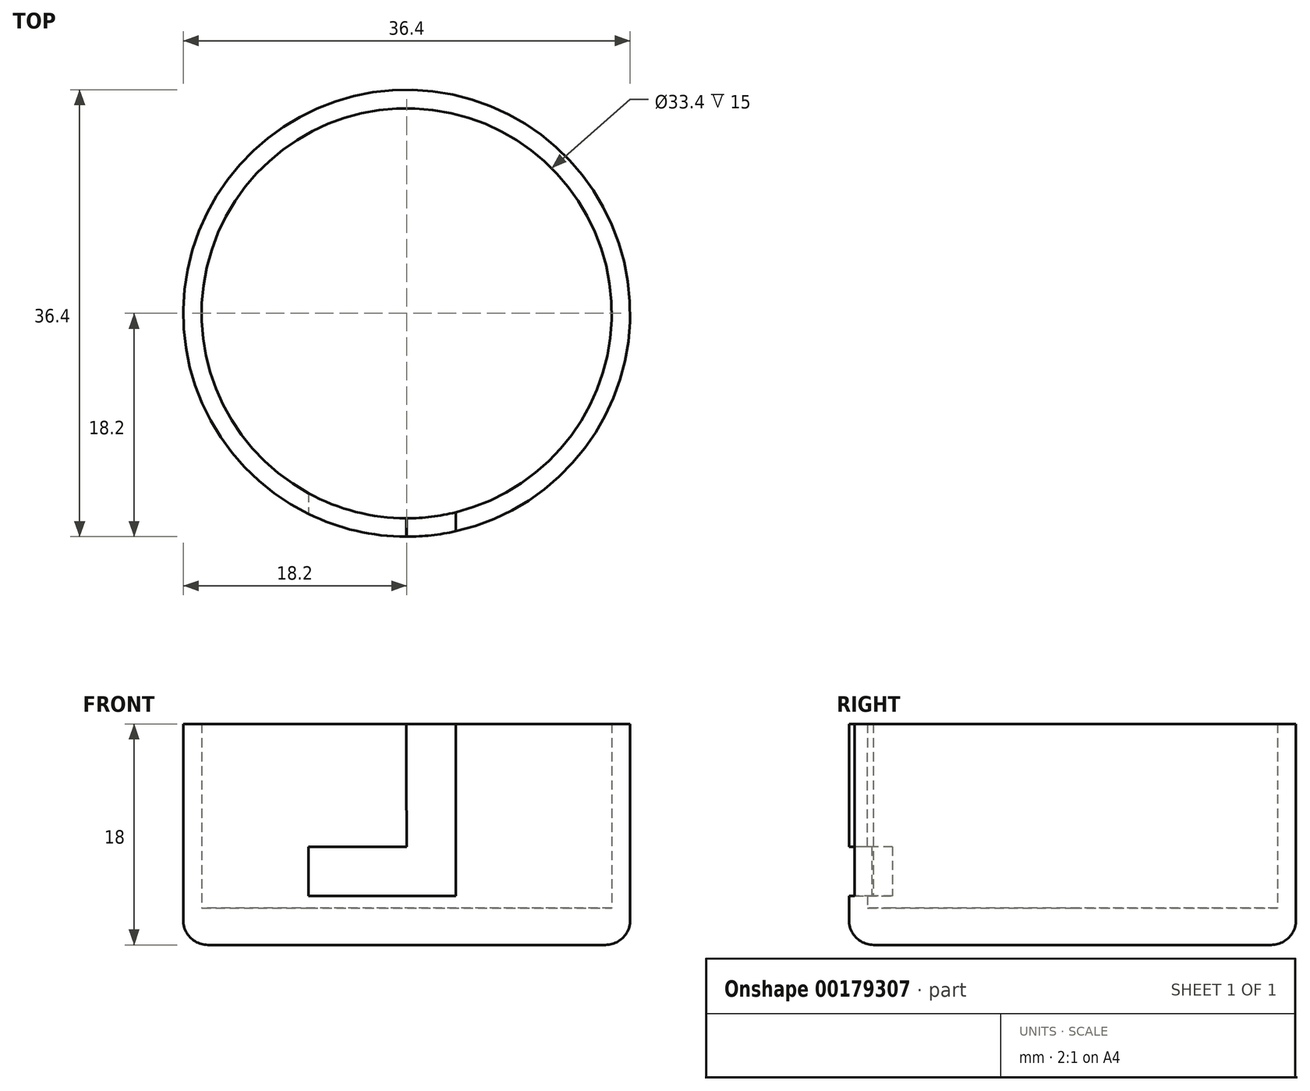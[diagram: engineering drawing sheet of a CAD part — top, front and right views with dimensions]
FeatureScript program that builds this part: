
annotation { "Feature Type Name" : "Feature", "Feature Type Description" : "" }
export const myFeature = defineFeature(function(context is Context, id is Id, definition is map)
    precondition{}
    {
        {
            var Q0;
            Q0=qCreatedBy(makeId("Top.planeOp"),FACE);
            var sketch = newSketch(context, id + "F0", { "sketchPlane" : qUnion([Q0])});
            skCircle(sketch, "E0", {"center": v(0, 0) * mm, "radius": 16.7 * mm});
            skCircle(sketch, "E1", {"center": v(0, 0) * mm, "radius": 18.2 * mm});
            skSolve(sketch);
        }
        {
            var Q0;
            Q0=makeQuery(id+"F0.imprint","IMPRINT",FACE,{"disambiguationData":[TD([[makeQuery(id+"F0.imprint","IMPRINT",EDGE,{"derivedFrom":sQuery(id+"F0.wireOp",EDGE,"E0")}),-1.0]])]});
            var Q1;
            Q1=makeQuery(id+"F0.imprint","IMPRINT",FACE,{"disambiguationData":[TD([[makeQuery(id+"F0.imprint","IMPRINT",EDGE,{"derivedFrom":sQuery(id+"F0.wireOp",EDGE,"E0")}),1.0]])]});
            extrude(context, id + "F1", {"entities" : qUnion([Q0, Q1]), "depth" : 3 * mm});
        }
        {
            var Q0;
            Q0=makeQuery(id+"F1.opExtrude","CAP_FACE",FACE,{"disambiguationData":[OSD([sQuery(id+"F0.wireOp",EDGE,"E1")])],"isStart":false});
            var sketch = newSketch(context, id + "F2", { "sketchPlane" : qUnion([Q0])});
            skCircle(sketch, "E2", {"center": v(0, 0) * mm, "radius": 16.7 * mm});
            skSolve(sketch);
        }
        {
            var Q0;
            Q0=makeQuery(id+"F2.imprint","IMPRINT",FACE,{"disambiguationData":[TD([[makeQuery(id+"F2.imprint","IMPRINT",EDGE,{"derivedFrom":sQuery(id+"F2.wireOp",EDGE,"E2")}),-1.0]])]});
            extrude(context, id + "F3", {"entities" : qUnion([Q0]), "operationType" : NewBodyOperationType.ADD, "depth" : 15 * mm});
        }
        {
            var Q0;
            Q0=qCreatedBy(makeId("Front.planeOp"),FACE);
            cPlane(context, id + "F4", {"entities" : qUnion([Q0]), "cplaneType" : CPlaneType.OFFSET, "offset" : 18.2 * mm, "width" : 150 * mm, "height" : 150 * mm});
        }
        {
            var Q0;
            Q0=qCreatedBy(id+"F4.planeOp",FACE);
            var sketch = newSketch(context, id + "F5", { "sketchPlane" : qUnion([Q0])});
            skLineSegment(sketch, "E3", {"start": v(0, 42.53) * mm, "end": v(0, -15.02) * mm, "construction": true});
            skLineSegment(sketch, "E4", {"start": v(0, 8) * mm, "end": v(-8, 8) * mm});
            skLineSegment(sketch, "E5", {"start": v(-8, 8) * mm, "end": v(-8, 4) * mm});
            skLineSegment(sketch, "E6", {"start": v(-8, 4) * mm, "end": v(4, 4) * mm});
            skLineSegment(sketch, "E7", {"start": v(4, 4) * mm, "end": v(4, 20) * mm});
            skLineSegment(sketch, "E8", {"start": v(-0.04, 16) * mm, "end": v(0, 8) * mm});
            skLineSegment(sketch, "E9", {"start": v(-0.04, 16) * mm, "end": v(-0.04, 20) * mm});
            skLineSegment(sketch, "E10", {"start": v(-0.04, 20) * mm, "end": v(3.96, 20) * mm});
            skLineSegment(sketch, "E11", {"start": v(3.96, 20) * mm, "end": v(4, 20) * mm});
            skSolve(sketch);
        }
        {
            var Q0;
            Q0 = qSketchRegion(id + "F5", true);
            extrude(context, id + "F6", {"entities" : qUnion([Q0]), "operationType" : NewBodyOperationType.REMOVE, "oppositeDirection" : true, "depth" : 10 * mm});
        }
        {
            var Q0;
            Q0=makeQuery(id+"F1.opExtrude","CAP_EDGE",EDGE,{"disambiguationData":[OSD([sQuery(id+"F0.wireOp",EDGE,"E1")])],"isStart":true});
            fillet(context, id + "F7", {"entities" : qUnion([Q0]), "radius" : 2 * mm, "tangentPropagation" : true, "allowEdgeOverflow" : false});
        }
    });
